# Revit family: BALANCE BEAM COMBO
name_source: partatom
category: Furniture Systems
units: mm (PartAtom-declared; Revit-internal decimal feet)

## family parameters
Always vertical = Yes
Cut with Voids When Loaded = No
Part Type = Normal
Room Calculation Point = No
Round Connector Dimension = Use Diameter
Shared = No
Work Plane-Based = No

## types (1)
- BALANCE BEAM COMBO
    BALANCE BEAM = FK041-48X18X9
    BALANCE BEAM CORNER = FK042-26X26X9
    Balance Beam Corner-1_Seat Fabric = <By Category>
    Balance Beam Corner-1_Side Fabric = <By Category>
    Balance Beam Corner-2_Seat Fabric = <By Category>
    Balance Beam Corner-2_Side Fabric = <By Category>
    Balance Beam-1_Seat Fabric = <By Category>
    Balance Beam-1_Side Fabric = <By Category>
    Balance Beam-2_Seat Fabric = <By Category>
    Balance Beam-2_Side Fabric = <By Category>
    Balance Beam-3_Seat Fabric = <By Category>
    Balance Beam-3_Side Fabric = <By Category>
    Description = Combo Products -BALANCE BEAM COMBO
    Manufacturer = FOMCORE
    Model = BALANCE BEAM COMBO
    URL = https://fomcore.com

## geometry (parser evidence)
native form markers: Sweep x2
no freeform markers — native parametric forms only
